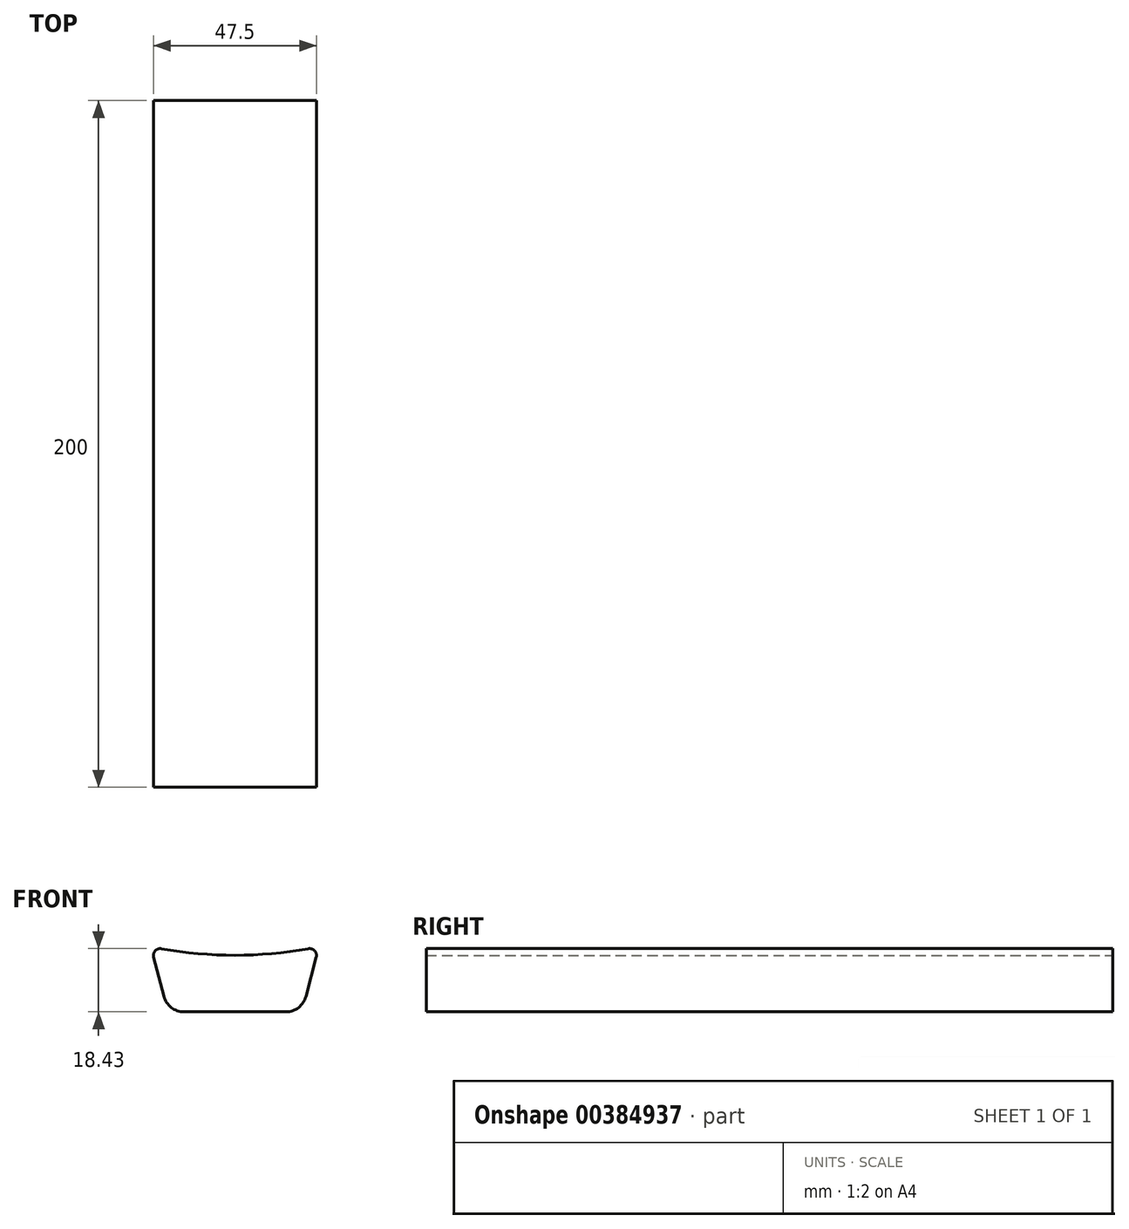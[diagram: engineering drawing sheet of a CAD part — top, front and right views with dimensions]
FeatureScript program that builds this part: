
annotation { "Feature Type Name" : "Feature", "Feature Type Description" : "" }
export const myFeature = defineFeature(function(context is Context, id is Id, definition is map)
    precondition{}
    {
        {
            var Q0;
            Q0=qCreatedBy(makeId("Front.planeOp"),FACE);
            var sketch = newSketch(context, id + "F0", { "sketchPlane" : qUnion([Q0])});
            skLineSegment(sketch, "E0.bottom", {"start": v(0, 0) * mm, "end": v(49, 0) * mm});
            skLineSegment(sketch, "E0.top", {"start": v(0, 19) * mm, "end": v(49, 19) * mm});
            skLineSegment(sketch, "E0.left", {"start": v(0, 0) * mm, "end": v(0, 19) * mm});
            skLineSegment(sketch, "E0.right", {"start": v(49, 0) * mm, "end": v(49, 19) * mm});
            skLineSegment(sketch, "E1", {"start": v(5, 0) * mm, "end": v(44, 0) * mm, "construction": true});
            skLineSegment(sketch, "E2", {"start": v(5, 0) * mm, "end": v(0, 19) * mm});
            skLineSegment(sketch, "E3", {"start": v(44, 0) * mm, "end": v(49, 19) * mm});
            skArc(sketch, "E4", {"start": v(0, 19) * mm, "mid": v(24.5, 16.47) * mm, "end": v(49, 19) * mm});
            skSolve(sketch);
        }
        {
            var Q0;
            {var subQ0=sQuery(id+"F0.wireOp",EDGE,"E2");Q0=makeQuery(id+"F0.imprint","IMPRINT",FACE,{"disambiguationData":[TD([[makeQuery(id+"F0.imprint","IMPRINT",EDGE,{"derivedFrom":subQ0}),-1.0]])]});}
            extrude(context, id + "F1", {"entities" : qUnion([Q0]), "depth" : 200 * mm});
        }
        {
            var Q0;
            Q0=makeQuery(id+"F1.opExtrude","SWEPT_EDGE",EDGE,{"disambiguationData":[OSD([sQuery(id+"F0.wireOp",EDGE,"E0.bottom"),sQuery(id+"F0.wireOp",EDGE,"E2")])]});
            var Q1;
            Q1=makeQuery(id+"F1.opExtrude","SWEPT_EDGE",EDGE,{"disambiguationData":[OSD([sQuery(id+"F0.wireOp",EDGE,"E0.bottom"),sQuery(id+"F0.wireOp",EDGE,"E3")])]});
            fillet(context, id + "F2", {"entities" : qUnion([Q0, Q1]), "radius" : 6 * mm, "tangentPropagation" : true, "allowEdgeOverflow" : false});
        }
        {
            var Q0;
            Q0=makeQuery(id+"F1.opExtrude","SWEPT_EDGE",EDGE,{"disambiguationData":[OSD([sQuery(id+"F0.wireOp",EDGE,"E0.top"),sQuery(id+"F0.wireOp",EDGE,"E0.right"),sQuery(id+"F0.wireOp",EDGE,"E3"),sQuery(id+"F0.wireOp",EDGE,"E4")])]});
            var Q1;
            Q1=makeQuery(id+"F1.opExtrude","SWEPT_EDGE",EDGE,{"disambiguationData":[OSD([sQuery(id+"F0.wireOp",EDGE,"E0.top"),sQuery(id+"F0.wireOp",EDGE,"E0.left"),sQuery(id+"F0.wireOp",EDGE,"E2"),sQuery(id+"F0.wireOp",EDGE,"E4")])]});
            fillet(context, id + "F3", {"entities" : qUnion([Q0, Q1]), "radius" : 2 * mm, "tangentPropagation" : true, "allowEdgeOverflow" : false});
        }
    });
